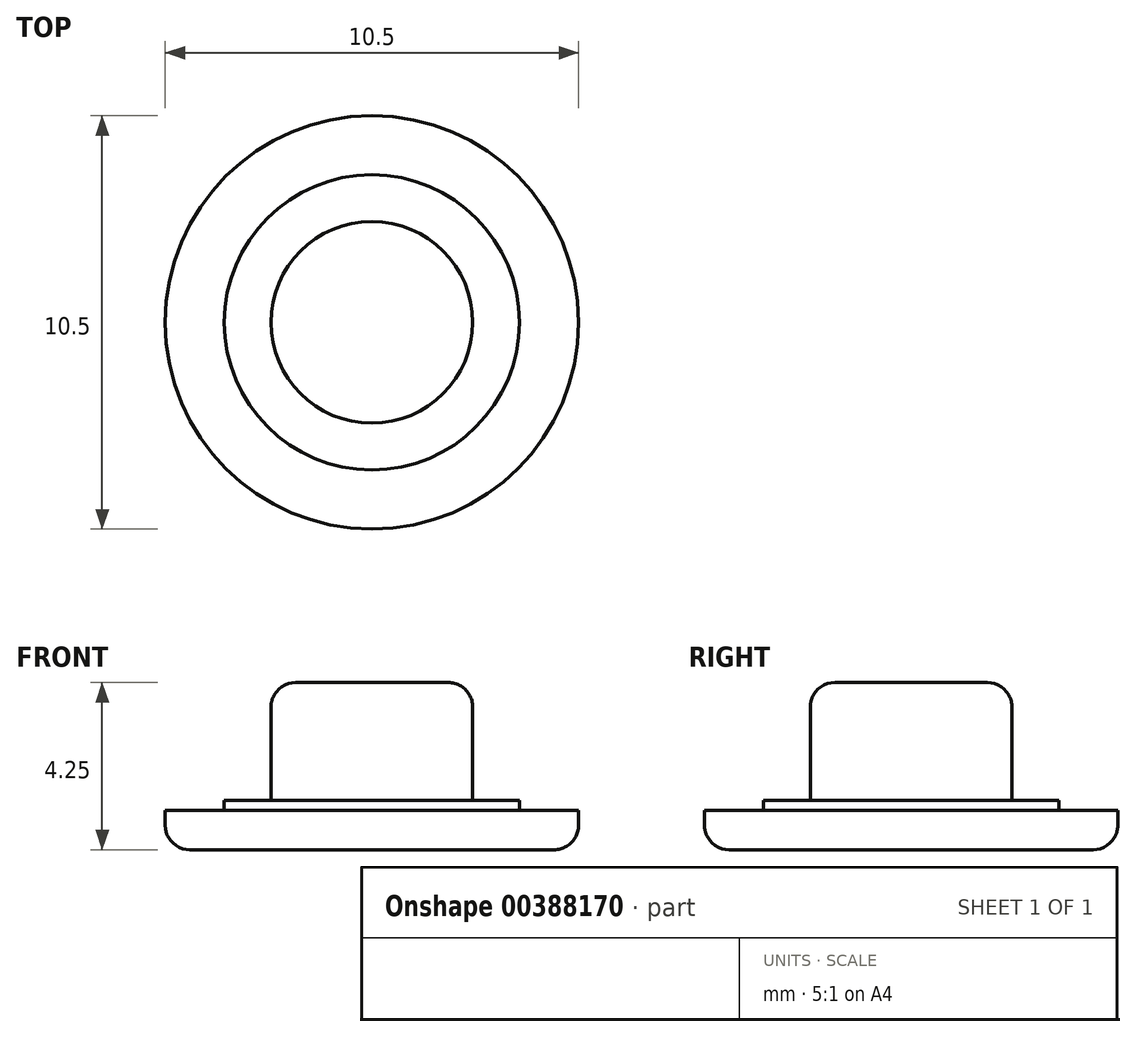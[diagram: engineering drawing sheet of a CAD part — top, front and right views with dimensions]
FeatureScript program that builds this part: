
annotation { "Feature Type Name" : "Feature", "Feature Type Description" : "" }
export const myFeature = defineFeature(function(context is Context, id is Id, definition is map)
    precondition{}
    {
        {
            var Q0;
            Q0=qCreatedBy(makeId("Top.planeOp"),FACE);
            var sketch = newSketch(context, id + "F0", { "sketchPlane" : qUnion([Q0])});
            skCircle(sketch, "E0", {"center": v(0, 0) * mm, "radius": 5.25 * mm});
            skCircle(sketch, "E1", {"center": v(0, 0) * mm, "radius": 3.75 * mm});
            skCircle(sketch, "E2", {"center": v(0, 0) * mm, "radius": 2.56 * mm});
            skSolve(sketch);
        }
        {
            var Q0;
            Q0=makeQuery(id+"F0.imprint","IMPRINT",FACE,{"disambiguationData":[TD([[makeQuery(id+"F0.imprint","IMPRINT",EDGE,{"derivedFrom":sQuery(id+"F0.wireOp",EDGE,"E2")}),1.0]])]});
            extrude(context, id + "F1", {"entities" : qUnion([Q0]), "depth" : 4.25 * mm, "offsetDistance" : 25 * mm});
        }
        {
            var Q0;
            Q0=makeQuery(id+"F0.imprint","IMPRINT",FACE,{"disambiguationData":[TD([[makeQuery(id+"F0.imprint","IMPRINT",EDGE,{"derivedFrom":sQuery(id+"F0.wireOp",EDGE,"E1")}),1.0]])]});
            extrude(context, id + "F2", {"entities" : qUnion([Q0]), "operationType" : NewBodyOperationType.ADD, "depth" : 1.25 * mm, "offsetDistance" : 25 * mm});
        }
        {
            var Q0;
            Q0=makeQuery(id+"F0.imprint","IMPRINT",FACE,{"disambiguationData":[TD([[makeQuery(id+"F0.imprint","IMPRINT",EDGE,{"derivedFrom":sQuery(id+"F0.wireOp",EDGE,"E0")}),1.0]])]});
            extrude(context, id + "F3", {"entities" : qUnion([Q0]), "operationType" : NewBodyOperationType.ADD, "depth" : 1 * mm, "offsetDistance" : 25 * mm});
        }
        {
            var Q0;
            Q0=makeQuery(id+"F3.opExtrude","CAP_EDGE",EDGE,{"disambiguationData":[OSD([sQuery(id+"F0.wireOp",EDGE,"E0")])],"isStart":true});
            var Q1;
            Q1=makeQuery(id+"F1.opExtrude","CAP_EDGE",EDGE,{"disambiguationData":[OSD([sQuery(id+"F0.wireOp",EDGE,"E2")])],"isStart":false});
            fillet(context, id + "F4", {"entities" : qUnion([Q0, Q1]), "radius" : .625 * mm, "tangentPropagation" : true, "allowEdgeOverflow" : false});
        }
    });
